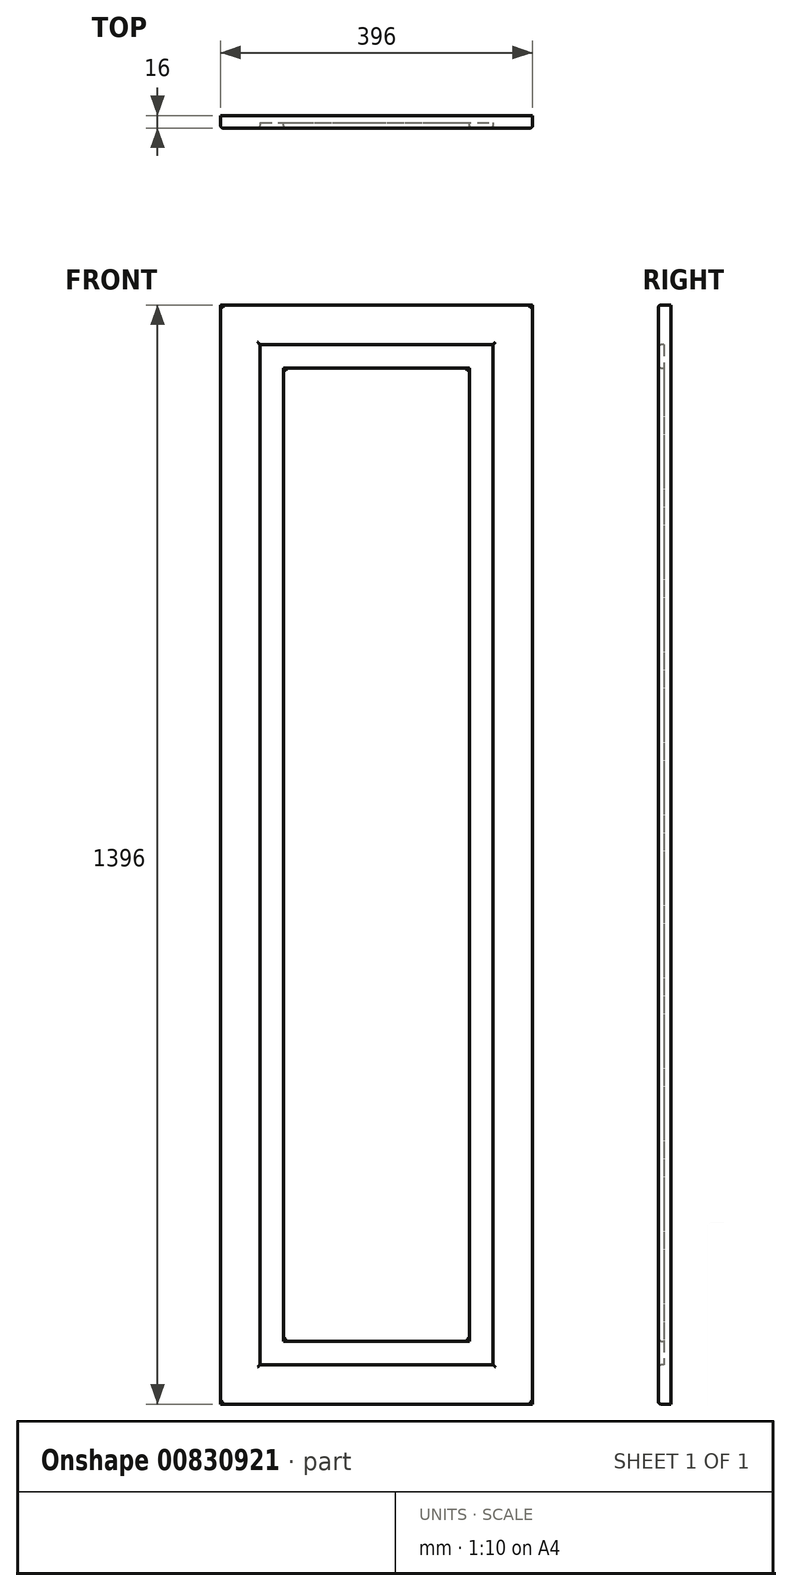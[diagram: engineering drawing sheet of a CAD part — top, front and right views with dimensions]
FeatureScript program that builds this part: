
annotation { "Feature Type Name" : "Feature", "Feature Type Description" : "" }
export const myFeature = defineFeature(function(context is Context, id is Id, definition is map)
    precondition{}
    {
        {
            var Q0;
            Q0=qCreatedBy(makeId("Front.planeOp"),FACE);
            var sketch = newSketch(context, id + "F0", { "sketchPlane" : qUnion([Q0])});
            skLineSegment(sketch, "E0.bottom", {"start": v(0, 0) * mm, "end": v(44.66, 0) * mm});
            skLineSegment(sketch, "E0.top", {"start": v(0, 33.8) * mm, "end": v(44.66, 33.8) * mm});
            skLineSegment(sketch, "E0.left", {"start": v(0, 0) * mm, "end": v(0, 33.8) * mm});
            skLineSegment(sketch, "E0.right", {"start": v(44.66, 0) * mm, "end": v(44.66, 33.8) * mm});
            skSolve(sketch);
        }
        {
            var Q0;
            Q0=makeQuery(id+"F0.imprint","IMPRINT",FACE,{"disambiguationData":[TD([[makeQuery(id+"F0.imprint","IMPRINT",EDGE,{"derivedFrom":sQuery(id+"F0.wireOp",EDGE,"E0.bottom")}),1.0]])]});
            extrude(context, id + "F1", {"entities" : qUnion([Q0]), "depth" : 16 * mm, "offsetDistance" : 25.4 * mm});
        }
        {
            var Q0;
            Q0=makeQuery(id+"F1.opExtrude","SWEPT_FACE",FACE,{"disambiguationData":[OSD([sQuery(id+"F0.wireOp",EDGE,"E0.bottom")])]});
            extrude(context, id + "F2", {"entities" : qUnion([Q0]), "operationType" : NewBodyOperationType.ADD, "oppositeDirection" : true, "depth" : 796 * mm, "offsetDistance" : 25 * mm});
        }
        {
            var Q0;
            {var subQ0=sQuery(id+"F0.wireOp",EDGE,"E0.left");Q0=makeQuery(id+"F2.boolean.opBoolean","MERGE",FACE,{"derivedFrom":[makeQuery(id+"F1.opExtrude","SWEPT_FACE",FACE,{"disambiguationData":[OSD([subQ0])]}),makeQuery(id+"F2.opExtrude","SWEPT_FACE",FACE,{"disambiguationData":[OSD([sQuery(id+"F0.wireOp",EDGE,"E0.bottom"),subQ0])]})]});}
            extrude(context, id + "F3", {"entities" : qUnion([Q0]), "operationType" : NewBodyOperationType.ADD, "oppositeDirection" : true, "depth" : 196 * mm, "offsetDistance" : 25 * mm});
        }
        {
            var Q0;
            {var subQ0=sQuery(id+"F0.wireOp",EDGE,"E0.left");var subQ1=sQuery(id+"F0.wireOp",EDGE,"E0.bottom");Q0=makeQuery(id+"F3.boolean.opBoolean","MERGE",FACE,{"derivedFrom":[makeQuery(id+"F2.boolean.opBoolean","MERGE",FACE,{"derivedFrom":[makeQuery(id+"F1.opExtrude","CAP_FACE",FACE,{"disambiguationData":[OSD([subQ1,sQuery(id+"F0.wireOp",EDGE,"E0.top"),subQ0,sQuery(id+"F0.wireOp",EDGE,"E0.right")])],"isStart":false}),makeQuery(id+"F2.opExtrude","SWEPT_FACE",FACE,{"disambiguationData":[OSD([subQ1]),TDD([makeQuery(id+"F1.opExtrude","CAP_EDGE",EDGE,{"disambiguationData":[OSD([subQ1])],"isStart":false})])]})]}),makeQuery(id+"F3.opExtrude","SWEPT_FACE",FACE,{"disambiguationData":[OSD([subQ1,subQ0]),TDD([makeQuery(id+"F2.boolean.opBoolean","MERGE",EDGE,{"derivedFrom":[makeQuery(id+"F1.opExtrude","CAP_EDGE",EDGE,{"disambiguationData":[OSD([subQ0])],"isStart":false}),makeQuery(id+"F2.opExtrude","SWEPT_EDGE",EDGE,{"disambiguationData":[OSD([subQ1,subQ0]),TDD([makeQuery(id+"F1.opExtrude","CAP_VERTEX",VERTEX,{"disambiguationData":[OSD([subQ1,subQ0])],"isStart":false})])]})]})])]})]});}
            var sketch = newSketch(context, id + "F4", { "sketchPlane" : qUnion([Q0])});
            skLineSegment(sketch, "E1.bottom", {"start": v(59.7, 646.67) * mm, "end": v(128.66, 646.67) * mm});
            skLineSegment(sketch, "E1.top", {"start": v(59.7, 152.97) * mm, "end": v(128.66, 152.97) * mm});
            skLineSegment(sketch, "E1.left", {"start": v(59.7, 646.67) * mm, "end": v(59.7, 152.97) * mm});
            skLineSegment(sketch, "E1.right", {"start": v(128.66, 646.67) * mm, "end": v(128.66, 152.97) * mm});
            skSolve(sketch);
        }
        {
            var Q0;
            Q0=makeQuery(id+"F4.imprint","IMPRINT",FACE,{"disambiguationData":[TD([[makeQuery(id+"F4.imprint","IMPRINT",EDGE,{"derivedFrom":sQuery(id+"F4.wireOp",EDGE,"E1.bottom")}),-1.0]])]});
            extrude(context, id + "F5", {"entities" : qUnion([Q0]), "operationType" : NewBodyOperationType.REMOVE, "oppositeDirection" : true, "depth" : 7 * mm, "offsetDistance" : 25 * mm});
        }
        {
            var Q0;
            Q0=makeQuery(id+"F5.boolean.opBoolean","COPY",FACE,{"derivedFrom":makeQuery(id+"F5.opExtrude","SWEPT_FACE",FACE,{"disambiguationData":[OSD([sQuery(id+"F4.wireOp",EDGE,"E1.left")])]})});
            extrude(context, id + "F6", {"entities" : qUnion([Q0]), "operationType" : NewBodyOperationType.REMOVE, "oppositeDirection" : true, "depth" : 9.7 * mm, "offsetDistance" : 25 * mm});
        }
        {
            var Q0;
            {var subQ0=sQuery(id+"F4.wireOp",EDGE,"E1.bottom");Q0=makeQuery(id+"F6.boolean.opBoolean","MERGE",FACE,{"derivedFrom":[makeQuery(id+"F5.boolean.opBoolean","COPY",FACE,{"derivedFrom":makeQuery(id+"F5.opExtrude","SWEPT_FACE",FACE,{"disambiguationData":[OSD([subQ0])]})}),makeQuery(id+"F6.opExtrude","SWEPT_FACE",FACE,{"disambiguationData":[OSD([subQ0,sQuery(id+"F4.wireOp",EDGE,"E1.left")])]})]});}
            extrude(context, id + "F7", {"entities" : qUnion([Q0]), "operationType" : NewBodyOperationType.ADD, "oppositeDirection" : true, "depth" : 99.33 * mm, "offsetDistance" : 25 * mm});
        }
        {
            var Q0;
            {var subQ0=sQuery(id+"F4.wireOp",EDGE,"E1.bottom");Q0=makeQuery(id+"F6.boolean.opBoolean","MERGE",FACE,{"derivedFrom":[makeQuery(id+"F5.boolean.opBoolean","COPY",FACE,{"derivedFrom":makeQuery(id+"F5.opExtrude","SWEPT_FACE",FACE,{"disambiguationData":[OSD([subQ0])]})}),makeQuery(id+"F6.opExtrude","SWEPT_FACE",FACE,{"disambiguationData":[OSD([subQ0,sQuery(id+"F4.wireOp",EDGE,"E1.left")])]})]});}
            extrude(context, id + "F8", {"entities" : qUnion([Q0]), "operationType" : NewBodyOperationType.REMOVE, "oppositeDirection" : true, "depth" : 99.33 * mm, "offsetDistance" : 25 * mm});
        }
        {
            var Q0;
            {var subQ0=sQuery(id+"F4.wireOp",EDGE,"E1.right");Q0=makeQuery(id+"F8.boolean.opBoolean","MERGE",FACE,{"derivedFrom":[makeQuery(id+"F5.boolean.opBoolean","COPY",FACE,{"derivedFrom":makeQuery(id+"F5.opExtrude","SWEPT_FACE",FACE,{"disambiguationData":[OSD([subQ0])]})}),makeQuery(id+"F8.opExtrude","SWEPT_FACE",FACE,{"disambiguationData":[OSD([sQuery(id+"F4.wireOp",EDGE,"E1.bottom"),subQ0])]})]});}
            extrude(context, id + "F9", {"entities" : qUnion([Q0]), "operationType" : NewBodyOperationType.REMOVE, "oppositeDirection" : true, "depth" : 17.34 * mm, "offsetDistance" : 25 * mm});
        }
        {
            var Q0;
            {var subQ0=sQuery(id+"F4.wireOp",EDGE,"E1.top");Q0=makeQuery(id+"F9.boolean.opBoolean","MERGE",FACE,{"derivedFrom":[makeQuery(id+"F6.boolean.opBoolean","MERGE",FACE,{"derivedFrom":[makeQuery(id+"F5.boolean.opBoolean","COPY",FACE,{"derivedFrom":makeQuery(id+"F5.opExtrude","SWEPT_FACE",FACE,{"disambiguationData":[OSD([subQ0])]})}),makeQuery(id+"F6.opExtrude","SWEPT_FACE",FACE,{"disambiguationData":[OSD([subQ0,sQuery(id+"F4.wireOp",EDGE,"E1.left")])]})]}),makeQuery(id+"F9.opExtrude","SWEPT_FACE",FACE,{"disambiguationData":[OSD([subQ0,sQuery(id+"F4.wireOp",EDGE,"E1.right")])]})]});}
            extrude(context, id + "F10", {"entities" : qUnion([Q0]), "operationType" : NewBodyOperationType.REMOVE, "oppositeDirection" : true, "depth" : 102.97 * mm, "offsetDistance" : 25 * mm});
        }
        {
            var Q0;
            {var subQ0=sQuery(id+"F4.wireOp",EDGE,"E1.right");var subQ1=sQuery(id+"F4.wireOp",EDGE,"E1.top");var subQ2=sQuery(id+"F4.wireOp",EDGE,"E1.left");var subQ3=sQuery(id+"F4.wireOp",EDGE,"E1.bottom");Q0=makeQuery(id+"F10.boolean.opBoolean","MERGE",FACE,{"derivedFrom":[makeQuery(id+"F9.boolean.opBoolean","MERGE",FACE,{"derivedFrom":[makeQuery(id+"F8.boolean.opBoolean","MERGE",FACE,{"derivedFrom":[makeQuery(id+"F6.boolean.opBoolean","MERGE",FACE,{"derivedFrom":[makeQuery(id+"F5.boolean.opBoolean","COPY",FACE,{"derivedFrom":makeQuery(id+"F5.opExtrude","CAP_FACE",FACE,{"disambiguationData":[OSD([subQ3,subQ1,subQ2,subQ0])],"isStart":false})}),makeQuery(id+"F6.opExtrude","SWEPT_FACE",FACE,{"disambiguationData":[OSD([subQ2]),TDD([makeQuery(id+"F5.boolean.opBoolean","COPY",EDGE,{"derivedFrom":makeQuery(id+"F5.opExtrude","CAP_EDGE",EDGE,{"disambiguationData":[OSD([subQ2])],"isStart":false})})])]})]}),makeQuery(id+"F8.opExtrude","SWEPT_FACE",FACE,{"disambiguationData":[OSD([subQ3,subQ2]),TDD([makeQuery(id+"F6.boolean.opBoolean","MERGE",EDGE,{"derivedFrom":[makeQuery(id+"F5.boolean.opBoolean","COPY",EDGE,{"derivedFrom":makeQuery(id+"F5.opExtrude","CAP_EDGE",EDGE,{"disambiguationData":[OSD([subQ3])],"isStart":false})}),makeQuery(id+"F6.opExtrude","SWEPT_EDGE",EDGE,{"disambiguationData":[OSD([subQ3,subQ2]),TDD([makeQuery(id+"F5.boolean.opBoolean","COPY",VERTEX,{"derivedFrom":makeQuery(id+"F5.opExtrude","CAP_VERTEX",VERTEX,{"disambiguationData":[OSD([subQ3,subQ2])],"isStart":false})})])]})]})])]})]}),makeQuery(id+"F9.opExtrude","SWEPT_FACE",FACE,{"disambiguationData":[OSD([subQ3,subQ0]),TDD([makeQuery(id+"F8.boolean.opBoolean","MERGE",EDGE,{"derivedFrom":[makeQuery(id+"F5.boolean.opBoolean","COPY",EDGE,{"derivedFrom":makeQuery(id+"F5.opExtrude","CAP_EDGE",EDGE,{"disambiguationData":[OSD([subQ0])],"isStart":false})}),makeQuery(id+"F8.opExtrude","SWEPT_EDGE",EDGE,{"disambiguationData":[OSD([subQ3,subQ0]),TDD([makeQuery(id+"F5.boolean.opBoolean","COPY",VERTEX,{"derivedFrom":makeQuery(id+"F5.opExtrude","CAP_VERTEX",VERTEX,{"disambiguationData":[OSD([subQ3,subQ0])],"isStart":false})})])]})]})])]})]}),makeQuery(id+"F10.opExtrude","SWEPT_FACE",FACE,{"disambiguationData":[OSD([subQ1,subQ2,subQ0]),TDD([makeQuery(id+"F9.boolean.opBoolean","MERGE",EDGE,{"derivedFrom":[makeQuery(id+"F6.boolean.opBoolean","MERGE",EDGE,{"derivedFrom":[makeQuery(id+"F5.boolean.opBoolean","COPY",EDGE,{"derivedFrom":makeQuery(id+"F5.opExtrude","CAP_EDGE",EDGE,{"disambiguationData":[OSD([subQ1])],"isStart":false})}),makeQuery(id+"F6.opExtrude","SWEPT_EDGE",EDGE,{"disambiguationData":[OSD([subQ1,subQ2]),TDD([makeQuery(id+"F5.boolean.opBoolean","COPY",VERTEX,{"derivedFrom":makeQuery(id+"F5.opExtrude","CAP_VERTEX",VERTEX,{"disambiguationData":[OSD([subQ1,subQ2])],"isStart":false})})])]})]}),makeQuery(id+"F9.opExtrude","SWEPT_EDGE",EDGE,{"disambiguationData":[OSD([subQ1,subQ0]),TDD([makeQuery(id+"F5.boolean.opBoolean","COPY",VERTEX,{"derivedFrom":makeQuery(id+"F5.opExtrude","CAP_VERTEX",VERTEX,{"disambiguationData":[OSD([subQ1,subQ0])],"isStart":false})})])]})]})])]})]});}
            var sketch = newSketch(context, id + "F11", { "sketchPlane" : qUnion([Q0])});
            skLineSegment(sketch, "E2.bottom", {"start": v(74.13, 678.73) * mm, "end": v(109.41, 678.73) * mm});
            skLineSegment(sketch, "E2.top", {"start": v(74.13, 186.63) * mm, "end": v(109.41, 186.63) * mm});
            skLineSegment(sketch, "E2.left", {"start": v(74.13, 678.73) * mm, "end": v(74.13, 186.63) * mm});
            skLineSegment(sketch, "E2.right", {"start": v(109.41, 678.73) * mm, "end": v(109.41, 186.63) * mm});
            skSolve(sketch);
        }
        {
            var Q0;
            Q0=makeQuery(id+"F11.imprint","IMPRINT",FACE,{"disambiguationData":[TD([[makeQuery(id+"F11.imprint","IMPRINT",EDGE,{"derivedFrom":sQuery(id+"F11.wireOp",EDGE,"E2.bottom")}),-1.0]])]});
            extrude(context, id + "F12", {"entities" : qUnion([Q0]), "operationType" : NewBodyOperationType.ADD, "depth" : 7 * mm, "offsetDistance" : 25 * mm});
        }
        {
            var Q0;
            Q0=makeQuery(id+"F12.opExtrude","SWEPT_FACE",FACE,{"disambiguationData":[OSD([sQuery(id+"F11.wireOp",EDGE,"E2.bottom")])]});
            extrude(context, id + "F13", {"entities" : qUnion([Q0]), "operationType" : NewBodyOperationType.ADD, "depth" : 37.27 * mm, "offsetDistance" : 25 * mm});
        }
        {
            var Q0;
            {var subQ0=sQuery(id+"F11.wireOp",EDGE,"E2.right");Q0=makeQuery(id+"F13.boolean.opBoolean","MERGE",FACE,{"derivedFrom":[makeQuery(id+"F12.opExtrude","SWEPT_FACE",FACE,{"disambiguationData":[OSD([subQ0])]}),makeQuery(id+"F13.opExtrude","SWEPT_FACE",FACE,{"disambiguationData":[OSD([sQuery(id+"F11.wireOp",EDGE,"E2.bottom"),subQ0])]})]});}
            extrude(context, id + "F14", {"entities" : qUnion([Q0]), "operationType" : NewBodyOperationType.ADD, "depth" : 6.58 * mm, "offsetDistance" : 25 * mm});
        }
        {
            var Q0;
            {var subQ0=sQuery(id+"F11.wireOp",EDGE,"E2.top");Q0=makeQuery(id+"F14.boolean.opBoolean","MERGE",FACE,{"derivedFrom":[makeQuery(id+"F12.opExtrude","SWEPT_FACE",FACE,{"disambiguationData":[OSD([subQ0])]}),makeQuery(id+"F14.opExtrude","SWEPT_FACE",FACE,{"disambiguationData":[OSD([subQ0,sQuery(id+"F11.wireOp",EDGE,"E2.right")])]})]});}
            extrude(context, id + "F15", {"entities" : qUnion([Q0]), "operationType" : NewBodyOperationType.ADD, "depth" : 106.63 * mm, "offsetDistance" : 25 * mm});
        }
        {
            var Q0;
            {var subQ0=sQuery(id+"F11.wireOp",EDGE,"E2.left");Q0=makeQuery(id+"F15.boolean.opBoolean","MERGE",FACE,{"derivedFrom":[makeQuery(id+"F13.boolean.opBoolean","MERGE",FACE,{"derivedFrom":[makeQuery(id+"F12.opExtrude","SWEPT_FACE",FACE,{"disambiguationData":[OSD([subQ0])]}),makeQuery(id+"F13.opExtrude","SWEPT_FACE",FACE,{"disambiguationData":[OSD([sQuery(id+"F11.wireOp",EDGE,"E2.bottom"),subQ0])]})]}),makeQuery(id+"F15.opExtrude","SWEPT_FACE",FACE,{"disambiguationData":[OSD([sQuery(id+"F11.wireOp",EDGE,"E2.top"),subQ0])]})]});}
            extrude(context, id + "F16", {"entities" : qUnion([Q0]), "operationType" : NewBodyOperationType.REMOVE, "oppositeDirection" : true, "depth" : 5.87 * mm, "offsetDistance" : 25 * mm});
        }
        {
            var Q0;
            Q0=makeQuery(id+"F3.opExtrude","CAP_FACE",FACE,{"disambiguationData":[OSD([sQuery(id+"F0.wireOp",EDGE,"E0.bottom"),sQuery(id+"F0.wireOp",EDGE,"E0.left")])],"isStart":false});
            extrude(context, id + "F17", {"entities" : qUnion([Q0]), "operationType" : NewBodyOperationType.ADD, "depth" : 200 * mm, "offsetDistance" : 25 * mm});
        }
        {
            var Q0;
            {var subQ0=sQuery(id+"F4.wireOp",EDGE,"E1.right");Q0=makeQuery(id+"F10.boolean.opBoolean","MERGE",FACE,{"derivedFrom":[makeQuery(id+"F9.boolean.opBoolean","COPY",FACE,{"derivedFrom":makeQuery(id+"F9.opExtrude","CAP_FACE",FACE,{"disambiguationData":[OSD([sQuery(id+"F4.wireOp",EDGE,"E1.bottom"),subQ0])],"isStart":false})}),makeQuery(id+"F10.opExtrude","SWEPT_FACE",FACE,{"disambiguationData":[OSD([sQuery(id+"F4.wireOp",EDGE,"E1.top"),subQ0])]})]});}
            extrude(context, id + "F18", {"entities" : qUnion([Q0]), "operationType" : NewBodyOperationType.REMOVE, "oppositeDirection" : true, "depth" : 200 * mm, "offsetDistance" : 25 * mm});
        }
        {
            var Q0;
            {var subQ0=sQuery(id+"F11.wireOp",EDGE,"E2.right");var subQ1=sQuery(id+"F11.wireOp",EDGE,"E2.top");Q0=makeQuery(id+"F15.boolean.opBoolean","MERGE",FACE,{"derivedFrom":[makeQuery(id+"F14.opExtrude","CAP_FACE",FACE,{"disambiguationData":[OSD([sQuery(id+"F11.wireOp",EDGE,"E2.bottom"),subQ0])],"isStart":false}),makeQuery(id+"F15.opExtrude","SWEPT_FACE",FACE,{"disambiguationData":[OSD([subQ1,subQ0]),TDD([makeQuery(id+"F14.opExtrude","CAP_EDGE",EDGE,{"disambiguationData":[OSD([subQ1,subQ0])],"isStart":false})])]})]});}
            extrude(context, id + "F19", {"entities" : qUnion([Q0]), "operationType" : NewBodyOperationType.ADD, "depth" : 200 * mm, "offsetDistance" : 25 * mm});
        }
        {
            var Q0;
            Q0=makeQuery(id+"F17.opExtrude","CAP_FACE",FACE,{"disambiguationData":[OSD([sQuery(id+"F0.wireOp",EDGE,"E0.bottom"),sQuery(id+"F0.wireOp",EDGE,"E0.left")])],"isStart":false});
            extrude(context, id + "F20", {"entities" : qUnion([Q0]), "operationType" : NewBodyOperationType.ADD, "depth" : 200 * mm, "offsetDistance" : 25 * mm});
        }
        {
            var Q0;
            Q0=makeQuery(id+"F18.boolean.opBoolean","COPY",FACE,{"derivedFrom":makeQuery(id+"F18.opExtrude","CAP_FACE",FACE,{"disambiguationData":[OSD([sQuery(id+"F4.wireOp",EDGE,"E1.bottom"),sQuery(id+"F4.wireOp",EDGE,"E1.top"),sQuery(id+"F4.wireOp",EDGE,"E1.right")])],"isStart":false})});
            extrude(context, id + "F21", {"entities" : qUnion([Q0]), "operationType" : NewBodyOperationType.REMOVE, "oppositeDirection" : true, "depth" : 200 * mm, "offsetDistance" : 25 * mm});
        }
        {
            var Q0;
            Q0=makeQuery(id+"F19.opExtrude","CAP_FACE",FACE,{"disambiguationData":[OSD([sQuery(id+"F11.wireOp",EDGE,"E2.bottom"),sQuery(id+"F11.wireOp",EDGE,"E2.top"),sQuery(id+"F11.wireOp",EDGE,"E2.right")])],"isStart":false});
            extrude(context, id + "F22", {"entities" : qUnion([Q0]), "operationType" : NewBodyOperationType.ADD, "depth" : 200 * mm, "offsetDistance" : 25 * mm});
        }
        {
            var Q0;
            Q0=makeQuery(id+"F20.opExtrude","CAP_FACE",FACE,{"disambiguationData":[OSD([sQuery(id+"F0.wireOp",EDGE,"E0.bottom"),sQuery(id+"F0.wireOp",EDGE,"E0.left")])],"isStart":false});
            extrude(context, id + "F23", {"entities" : qUnion([Q0]), "operationType" : NewBodyOperationType.ADD, "depth" : 400 * mm, "offsetDistance" : 25 * mm});
        }
        {
            var Q0;
            Q0=makeQuery(id+"F21.boolean.opBoolean","COPY",FACE,{"derivedFrom":makeQuery(id+"F21.opExtrude","CAP_FACE",FACE,{"disambiguationData":[OSD([sQuery(id+"F4.wireOp",EDGE,"E1.bottom"),sQuery(id+"F4.wireOp",EDGE,"E1.top"),sQuery(id+"F4.wireOp",EDGE,"E1.right")])],"isStart":false})});
            extrude(context, id + "F24", {"entities" : qUnion([Q0]), "operationType" : NewBodyOperationType.REMOVE, "oppositeDirection" : true, "depth" : 400 * mm, "offsetDistance" : 25 * mm});
        }
        {
            var Q0;
            Q0=makeQuery(id+"F22.opExtrude","CAP_FACE",FACE,{"disambiguationData":[OSD([sQuery(id+"F11.wireOp",EDGE,"E2.bottom"),sQuery(id+"F11.wireOp",EDGE,"E2.top"),sQuery(id+"F11.wireOp",EDGE,"E2.right")])],"isStart":false});
            extrude(context, id + "F25", {"entities" : qUnion([Q0]), "operationType" : NewBodyOperationType.ADD, "depth" : 400 * mm, "offsetDistance" : 25 * mm});
        }
        {
            var Q0;
            {var subQ0=sQuery(id+"F11.wireOp",EDGE,"E2.right");var subQ1=sQuery(id+"F11.wireOp",EDGE,"E2.top");Q0=makeQuery(id+"F25.boolean.opBoolean","MERGE",FACE,{"derivedFrom":[makeQuery(id+"F22.boolean.opBoolean","MERGE",FACE,{"derivedFrom":[makeQuery(id+"F19.boolean.opBoolean","MERGE",FACE,{"derivedFrom":[makeQuery(id+"F15.opExtrude","CAP_FACE",FACE,{"disambiguationData":[OSD([subQ1,subQ0])],"isStart":false}),makeQuery(id+"F19.opExtrude","SWEPT_FACE",FACE,{"disambiguationData":[OSD([subQ1,subQ0])]})]}),makeQuery(id+"F22.opExtrude","SWEPT_FACE",FACE,{"disambiguationData":[OSD([subQ1,subQ0])]})]}),makeQuery(id+"F25.opExtrude","SWEPT_FACE",FACE,{"disambiguationData":[OSD([subQ1,subQ0])]})]});}
            extrude(context, id + "F26", {"entities" : qUnion([Q0]), "operationType" : NewBodyOperationType.REMOVE, "oppositeDirection" : true, "depth" : 400 * mm, "offsetDistance" : 25 * mm});
        }
        {
            var Q0;
            {var subQ0=sQuery(id+"F4.wireOp",EDGE,"E1.right");var subQ1=sQuery(id+"F4.wireOp",EDGE,"E1.top");Q0=makeQuery(id+"F24.boolean.opBoolean","MERGE",FACE,{"derivedFrom":[makeQuery(id+"F21.boolean.opBoolean","MERGE",FACE,{"derivedFrom":[makeQuery(id+"F18.boolean.opBoolean","MERGE",FACE,{"derivedFrom":[makeQuery(id+"F10.boolean.opBoolean","COPY",FACE,{"derivedFrom":makeQuery(id+"F10.opExtrude","CAP_FACE",FACE,{"disambiguationData":[OSD([subQ1,sQuery(id+"F4.wireOp",EDGE,"E1.left"),subQ0])],"isStart":false})}),makeQuery(id+"F18.opExtrude","SWEPT_FACE",FACE,{"disambiguationData":[OSD([subQ1,subQ0])]})]}),makeQuery(id+"F21.opExtrude","SWEPT_FACE",FACE,{"disambiguationData":[OSD([subQ1,subQ0])]})]}),makeQuery(id+"F24.opExtrude","SWEPT_FACE",FACE,{"disambiguationData":[OSD([subQ1,subQ0])]})]});}
            extrude(context, id + "F27", {"entities" : qUnion([Q0]), "operationType" : NewBodyOperationType.ADD, "depth" : 400 * mm, "offsetDistance" : 25 * mm});
        }
        {
            var Q0;
            {var subQ0=sQuery(id+"F0.wireOp",EDGE,"E0.left");var subQ1=sQuery(id+"F0.wireOp",EDGE,"E0.bottom");var subQ2=makeQuery(id+"F1.opExtrude","SWEPT_EDGE",EDGE,{"disambiguationData":[OSD([subQ1,subQ0])]});var subQ3=makeQuery(id+"F3.opExtrude","CAP_EDGE",EDGE,{"disambiguationData":[OSD([subQ1,subQ0]),TDD([subQ2])],"isStart":false});var subQ4=makeQuery(id+"F17.opExtrude","CAP_EDGE",EDGE,{"disambiguationData":[OSD([subQ1,subQ0]),TDD([subQ3])],"isStart":false});Q0=makeQuery(id+"F23.boolean.opBoolean","MERGE",FACE,{"derivedFrom":[makeQuery(id+"F20.boolean.opBoolean","MERGE",FACE,{"derivedFrom":[makeQuery(id+"F17.boolean.opBoolean","MERGE",FACE,{"derivedFrom":[makeQuery(id+"F3.boolean.opBoolean","MERGE",FACE,{"derivedFrom":[makeQuery(id+"F1.opExtrude","SWEPT_FACE",FACE,{"disambiguationData":[OSD([subQ1])]}),makeQuery(id+"F3.opExtrude","SWEPT_FACE",FACE,{"disambiguationData":[OSD([subQ1,subQ0]),TDD([subQ2])]})]}),makeQuery(id+"F17.opExtrude","SWEPT_FACE",FACE,{"disambiguationData":[OSD([subQ1,subQ0]),TDD([subQ3])]})]}),makeQuery(id+"F20.opExtrude","SWEPT_FACE",FACE,{"disambiguationData":[OSD([subQ1,subQ0]),TDD([subQ4])]})]}),makeQuery(id+"F23.opExtrude","SWEPT_FACE",FACE,{"disambiguationData":[OSD([subQ1,subQ0]),TDD([makeQuery(id+"F20.opExtrude","CAP_EDGE",EDGE,{"disambiguationData":[OSD([subQ1,subQ0]),TDD([subQ4])],"isStart":false})])]})]});}
            extrude(context, id + "F28", {"entities" : qUnion([Q0]), "operationType" : NewBodyOperationType.REMOVE, "oppositeDirection" : true, "depth" : 400 * mm, "offsetDistance" : 25 * mm});
        }
        {
            var Q0;
            Q0=makeQuery(id+"F23.opExtrude","CAP_FACE",FACE,{"disambiguationData":[OSD([sQuery(id+"F0.wireOp",EDGE,"E0.bottom"),sQuery(id+"F0.wireOp",EDGE,"E0.left")])],"isStart":false});
            extrude(context, id + "F29", {"entities" : qUnion([Q0]), "operationType" : NewBodyOperationType.ADD, "depth" : 400 * mm, "offsetDistance" : 25 * mm});
        }
        {
            var Q0;
            Q0=makeQuery(id+"F24.boolean.opBoolean","COPY",FACE,{"derivedFrom":makeQuery(id+"F24.opExtrude","CAP_FACE",FACE,{"disambiguationData":[OSD([sQuery(id+"F4.wireOp",EDGE,"E1.bottom"),sQuery(id+"F4.wireOp",EDGE,"E1.top"),sQuery(id+"F4.wireOp",EDGE,"E1.right")])],"isStart":false})});
            extrude(context, id + "F30", {"entities" : qUnion([Q0]), "operationType" : NewBodyOperationType.REMOVE, "oppositeDirection" : true, "depth" : 400 * mm, "offsetDistance" : 25 * mm});
        }
        {
            var Q0;
            Q0=makeQuery(id+"F25.opExtrude","CAP_FACE",FACE,{"disambiguationData":[OSD([sQuery(id+"F11.wireOp",EDGE,"E2.bottom"),sQuery(id+"F11.wireOp",EDGE,"E2.top"),sQuery(id+"F11.wireOp",EDGE,"E2.right")])],"isStart":false});
            extrude(context, id + "F31", {"entities" : qUnion([Q0]), "operationType" : NewBodyOperationType.ADD, "depth" : 400 * mm, "offsetDistance" : 25 * mm});
        }
        {
            var Q0;
            Q0=makeQuery(id+"F31.opExtrude","CAP_FACE",FACE,{"disambiguationData":[OSD([sQuery(id+"F11.wireOp",EDGE,"E2.bottom"),sQuery(id+"F11.wireOp",EDGE,"E2.top"),sQuery(id+"F11.wireOp",EDGE,"E2.right")])],"isStart":false});
            extrude(context, id + "F32", {"entities" : qUnion([Q0]), "operationType" : NewBodyOperationType.REMOVE, "oppositeDirection" : true, "depth" : 1000 * mm, "offsetDistance" : 25 * mm});
        }
        {
            var Q0;
            Q0=makeQuery(id+"F30.boolean.opBoolean","COPY",FACE,{"derivedFrom":makeQuery(id+"F30.opExtrude","CAP_FACE",FACE,{"disambiguationData":[OSD([sQuery(id+"F4.wireOp",EDGE,"E1.bottom"),sQuery(id+"F4.wireOp",EDGE,"E1.top"),sQuery(id+"F4.wireOp",EDGE,"E1.right")])],"isStart":false})});
            extrude(context, id + "F33", {"entities" : qUnion([Q0]), "operationType" : NewBodyOperationType.ADD, "depth" : 1000 * mm, "offsetDistance" : 25 * mm});
        }
        {
            var Q0;
            Q0=makeQuery(id+"F29.opExtrude","CAP_FACE",FACE,{"disambiguationData":[OSD([sQuery(id+"F0.wireOp",EDGE,"E0.bottom"),sQuery(id+"F0.wireOp",EDGE,"E0.left")])],"isStart":false});
            extrude(context, id + "F34", {"entities" : qUnion([Q0]), "operationType" : NewBodyOperationType.REMOVE, "oppositeDirection" : true, "depth" : 1000 * mm, "offsetDistance" : 25 * mm});
        }
        {
            var Q0;
            {var subQ0=sQuery(id+"F0.wireOp",EDGE,"E0.left");var subQ1=sQuery(id+"F0.wireOp",EDGE,"E0.bottom");var subQ2=makeQuery(id+"F2.opExtrude","CAP_EDGE",EDGE,{"disambiguationData":[OSD([subQ1,subQ0])],"isStart":false});var subQ3=makeQuery(id+"F3.opExtrude","CAP_EDGE",EDGE,{"disambiguationData":[OSD([subQ1,subQ0]),TDD([subQ2])],"isStart":false});var subQ4=makeQuery(id+"F17.opExtrude","CAP_EDGE",EDGE,{"disambiguationData":[OSD([subQ1,subQ0]),TDD([subQ3])],"isStart":false});var subQ5=makeQuery(id+"F20.opExtrude","CAP_EDGE",EDGE,{"disambiguationData":[OSD([subQ1,subQ0]),TDD([subQ4])],"isStart":false});Q0=makeQuery(id+"F29.boolean.opBoolean","MERGE",FACE,{"derivedFrom":[makeQuery(id+"F23.boolean.opBoolean","MERGE",FACE,{"derivedFrom":[makeQuery(id+"F20.boolean.opBoolean","MERGE",FACE,{"derivedFrom":[makeQuery(id+"F17.boolean.opBoolean","MERGE",FACE,{"derivedFrom":[makeQuery(id+"F3.boolean.opBoolean","MERGE",FACE,{"derivedFrom":[makeQuery(id+"F2.opExtrude","CAP_FACE",FACE,{"disambiguationData":[OSD([subQ1])],"isStart":false}),makeQuery(id+"F3.opExtrude","SWEPT_FACE",FACE,{"disambiguationData":[OSD([subQ1,subQ0]),TDD([subQ2])]})]}),makeQuery(id+"F17.opExtrude","SWEPT_FACE",FACE,{"disambiguationData":[OSD([subQ1,subQ0]),TDD([subQ3])]})]}),makeQuery(id+"F20.opExtrude","SWEPT_FACE",FACE,{"disambiguationData":[OSD([subQ1,subQ0]),TDD([subQ4])]})]}),makeQuery(id+"F23.opExtrude","SWEPT_FACE",FACE,{"disambiguationData":[OSD([subQ1,subQ0]),TDD([subQ5])]})]}),makeQuery(id+"F29.opExtrude","SWEPT_FACE",FACE,{"disambiguationData":[OSD([subQ1,subQ0]),TDD([makeQuery(id+"F23.opExtrude","CAP_EDGE",EDGE,{"disambiguationData":[OSD([subQ1,subQ0]),TDD([subQ5])],"isStart":false})])]})]});}
            extrude(context, id + "F35", {"entities" : qUnion([Q0]), "operationType" : NewBodyOperationType.ADD, "depth" : 1000 * mm, "offsetDistance" : 25 * mm});
        }
        {
            var Q0;
            {var subQ0=sQuery(id+"F4.wireOp",EDGE,"E1.right");var subQ1=sQuery(id+"F4.wireOp",EDGE,"E1.bottom");Q0=makeQuery(id+"F30.boolean.opBoolean","MERGE",FACE,{"derivedFrom":[makeQuery(id+"F24.boolean.opBoolean","MERGE",FACE,{"derivedFrom":[makeQuery(id+"F21.boolean.opBoolean","MERGE",FACE,{"derivedFrom":[makeQuery(id+"F18.boolean.opBoolean","MERGE",FACE,{"derivedFrom":[makeQuery(id+"F9.boolean.opBoolean","MERGE",FACE,{"derivedFrom":[makeQuery(id+"F8.boolean.opBoolean","COPY",FACE,{"derivedFrom":makeQuery(id+"F8.opExtrude","CAP_FACE",FACE,{"disambiguationData":[OSD([subQ1,sQuery(id+"F4.wireOp",EDGE,"E1.left")])],"isStart":false})}),makeQuery(id+"F9.opExtrude","SWEPT_FACE",FACE,{"disambiguationData":[OSD([subQ1,subQ0]),TDD([makeQuery(id+"F8.boolean.opBoolean","COPY",EDGE,{"derivedFrom":makeQuery(id+"F8.opExtrude","CAP_EDGE",EDGE,{"disambiguationData":[OSD([subQ1,subQ0])],"isStart":false})})])]})]}),makeQuery(id+"F18.opExtrude","SWEPT_FACE",FACE,{"disambiguationData":[OSD([subQ1,subQ0])]})]}),makeQuery(id+"F21.opExtrude","SWEPT_FACE",FACE,{"disambiguationData":[OSD([subQ1,subQ0])]})]}),makeQuery(id+"F24.opExtrude","SWEPT_FACE",FACE,{"disambiguationData":[OSD([subQ1,subQ0])]})]}),makeQuery(id+"F30.opExtrude","SWEPT_FACE",FACE,{"disambiguationData":[OSD([subQ1,subQ0])]})]});}
            extrude(context, id + "F36", {"entities" : qUnion([Q0]), "operationType" : NewBodyOperationType.REMOVE, "oppositeDirection" : true, "depth" : 1000 * mm, "offsetDistance" : 25 * mm});
        }
        {
            var Q0;
            {var subQ0=sQuery(id+"F11.wireOp",EDGE,"E2.right");var subQ1=sQuery(id+"F11.wireOp",EDGE,"E2.bottom");Q0=makeQuery(id+"F31.boolean.opBoolean","MERGE",FACE,{"derivedFrom":[makeQuery(id+"F25.boolean.opBoolean","MERGE",FACE,{"derivedFrom":[makeQuery(id+"F22.boolean.opBoolean","MERGE",FACE,{"derivedFrom":[makeQuery(id+"F19.boolean.opBoolean","MERGE",FACE,{"derivedFrom":[makeQuery(id+"F14.boolean.opBoolean","MERGE",FACE,{"derivedFrom":[makeQuery(id+"F13.opExtrude","CAP_FACE",FACE,{"disambiguationData":[OSD([subQ1])],"isStart":false}),makeQuery(id+"F14.opExtrude","SWEPT_FACE",FACE,{"disambiguationData":[OSD([subQ1,subQ0]),TDD([makeQuery(id+"F13.opExtrude","CAP_EDGE",EDGE,{"disambiguationData":[OSD([subQ1,subQ0])],"isStart":false})])]})]}),makeQuery(id+"F19.opExtrude","SWEPT_FACE",FACE,{"disambiguationData":[OSD([subQ1,subQ0])]})]}),makeQuery(id+"F22.opExtrude","SWEPT_FACE",FACE,{"disambiguationData":[OSD([subQ1,subQ0])]})]}),makeQuery(id+"F25.opExtrude","SWEPT_FACE",FACE,{"disambiguationData":[OSD([subQ1,subQ0])]})]}),makeQuery(id+"F31.opExtrude","SWEPT_FACE",FACE,{"disambiguationData":[OSD([subQ1,subQ0])]})]});}
            extrude(context, id + "F37", {"entities" : qUnion([Q0]), "operationType" : NewBodyOperationType.ADD, "depth" : 1000 * mm, "offsetDistance" : 25 * mm});
        }
        {
            var Q0;
            {var subQ0=sQuery(id+"F11.wireOp",EDGE,"E2.right");var subQ1=sQuery(id+"F11.wireOp",EDGE,"E2.bottom");var subQ2=makeQuery(id+"F12.opExtrude","CAP_VERTEX",VERTEX,{"disambiguationData":[OSD([subQ1,subQ0])],"isStart":false});var subQ3=makeQuery(id+"F13.opExtrude","CAP_VERTEX",VERTEX,{"disambiguationData":[OSD([subQ1,subQ0]),TDD([subQ2])],"isStart":false});var subQ4=makeQuery(id+"F14.opExtrude","CAP_VERTEX",VERTEX,{"disambiguationData":[OSD([subQ1,subQ0]),TDD([subQ3])],"isStart":false});var subQ5=makeQuery(id+"F19.opExtrude","CAP_VERTEX",VERTEX,{"disambiguationData":[OSD([subQ1,subQ0]),TDD([subQ4])],"isStart":false});var subQ6=makeQuery(id+"F22.opExtrude","CAP_VERTEX",VERTEX,{"disambiguationData":[OSD([subQ1,subQ0]),TDD([subQ5])],"isStart":false});var subQ7=makeQuery(id+"F12.opExtrude","CAP_EDGE",EDGE,{"disambiguationData":[OSD([subQ1])],"isStart":false});var subQ8=sQuery(id+"F11.wireOp",EDGE,"E2.top");var subQ9=makeQuery(id+"F12.opExtrude","CAP_VERTEX",VERTEX,{"disambiguationData":[OSD([subQ8,subQ0])],"isStart":false});var subQ10=makeQuery(id+"F13.boolean.opBoolean","MERGE",EDGE,{"derivedFrom":[makeQuery(id+"F12.opExtrude","CAP_EDGE",EDGE,{"disambiguationData":[OSD([subQ0])],"isStart":false}),makeQuery(id+"F13.opExtrude","SWEPT_EDGE",EDGE,{"disambiguationData":[OSD([subQ1,subQ0]),TDD([subQ2])]})]});var subQ11=makeQuery(id+"F15.boolean.opBoolean","MERGE",EDGE,{"derivedFrom":[makeQuery(id+"F14.opExtrude","CAP_EDGE",EDGE,{"disambiguationData":[OSD([subQ1,subQ0]),TDD([subQ10])],"isStart":false}),makeQuery(id+"F15.opExtrude","SWEPT_EDGE",EDGE,{"disambiguationData":[OSD([subQ8,subQ0]),TDD([makeQuery(id+"F14.opExtrude","CAP_VERTEX",VERTEX,{"disambiguationData":[OSD([subQ8,subQ0]),TDD([subQ9])],"isStart":false})])]})]});var subQ12=makeQuery(id+"F19.opExtrude","CAP_EDGE",EDGE,{"disambiguationData":[OSD([subQ1,subQ8,subQ0]),TDD([subQ11])],"isStart":false});var subQ13=makeQuery(id+"F22.opExtrude","CAP_EDGE",EDGE,{"disambiguationData":[OSD([subQ1,subQ8,subQ0]),TDD([subQ12])],"isStart":false});Q0=makeQuery(id+"F37.boolean.opBoolean","MERGE",FACE,{"derivedFrom":[makeQuery(id+"F31.boolean.opBoolean","MERGE",FACE,{"derivedFrom":[makeQuery(id+"F25.boolean.opBoolean","MERGE",FACE,{"derivedFrom":[makeQuery(id+"F22.boolean.opBoolean","MERGE",FACE,{"derivedFrom":[makeQuery(id+"F19.boolean.opBoolean","MERGE",FACE,{"derivedFrom":[makeQuery(id+"F15.boolean.opBoolean","MERGE",FACE,{"derivedFrom":[makeQuery(id+"F14.boolean.opBoolean","MERGE",FACE,{"derivedFrom":[makeQuery(id+"F13.boolean.opBoolean","MERGE",FACE,{"derivedFrom":[makeQuery(id+"F12.opExtrude","CAP_FACE",FACE,{"disambiguationData":[OSD([subQ1,subQ8,sQuery(id+"F11.wireOp",EDGE,"E2.left"),subQ0])],"isStart":false}),makeQuery(id+"F13.opExtrude","SWEPT_FACE",FACE,{"disambiguationData":[OSD([subQ1]),TDD([subQ7])]})]}),makeQuery(id+"F14.opExtrude","SWEPT_FACE",FACE,{"disambiguationData":[OSD([subQ1,subQ0]),TDD([subQ10])]})]}),makeQuery(id+"F15.opExtrude","SWEPT_FACE",FACE,{"disambiguationData":[OSD([subQ8,subQ0]),TDD([makeQuery(id+"F14.boolean.opBoolean","MERGE",EDGE,{"derivedFrom":[makeQuery(id+"F12.opExtrude","CAP_EDGE",EDGE,{"disambiguationData":[OSD([subQ8])],"isStart":false}),makeQuery(id+"F14.opExtrude","SWEPT_EDGE",EDGE,{"disambiguationData":[OSD([subQ8,subQ0]),TDD([subQ9])]})]})])]})]}),makeQuery(id+"F19.opExtrude","SWEPT_FACE",FACE,{"disambiguationData":[OSD([subQ1,subQ8,subQ0]),TDD([subQ11])]})]}),makeQuery(id+"F22.opExtrude","SWEPT_FACE",FACE,{"disambiguationData":[OSD([subQ1,subQ8,subQ0]),TDD([subQ12])]})]}),makeQuery(id+"F25.opExtrude","SWEPT_FACE",FACE,{"disambiguationData":[OSD([subQ1,subQ8,subQ0]),TDD([subQ13])]})]}),makeQuery(id+"F31.opExtrude","SWEPT_FACE",FACE,{"disambiguationData":[OSD([subQ1,subQ8,subQ0]),TDD([makeQuery(id+"F25.opExtrude","CAP_EDGE",EDGE,{"disambiguationData":[OSD([subQ1,subQ8,subQ0]),TDD([subQ13])],"isStart":false})])]})]}),makeQuery(id+"F37.opExtrude","SWEPT_FACE",FACE,{"disambiguationData":[OSD([subQ1,subQ0]),TDD([makeQuery(id+"F31.boolean.opBoolean","MERGE",EDGE,{"derivedFrom":[makeQuery(id+"F25.boolean.opBoolean","MERGE",EDGE,{"derivedFrom":[makeQuery(id+"F22.boolean.opBoolean","MERGE",EDGE,{"derivedFrom":[makeQuery(id+"F19.boolean.opBoolean","MERGE",EDGE,{"derivedFrom":[makeQuery(id+"F14.boolean.opBoolean","MERGE",EDGE,{"derivedFrom":[makeQuery(id+"F13.opExtrude","CAP_EDGE",EDGE,{"disambiguationData":[OSD([subQ1]),TDD([subQ7])],"isStart":false}),makeQuery(id+"F14.opExtrude","SWEPT_EDGE",EDGE,{"disambiguationData":[OSD([subQ1,subQ0]),TDD([subQ3])]})]}),makeQuery(id+"F19.opExtrude","SWEPT_EDGE",EDGE,{"disambiguationData":[OSD([subQ1,subQ0]),TDD([subQ4])]})]}),makeQuery(id+"F22.opExtrude","SWEPT_EDGE",EDGE,{"disambiguationData":[OSD([subQ1,subQ0]),TDD([subQ5])]})]}),makeQuery(id+"F25.opExtrude","SWEPT_EDGE",EDGE,{"disambiguationData":[OSD([subQ1,subQ0]),TDD([subQ6])]})]}),makeQuery(id+"F31.opExtrude","SWEPT_EDGE",EDGE,{"disambiguationData":[OSD([subQ1,subQ0]),TDD([makeQuery(id+"F25.opExtrude","CAP_VERTEX",VERTEX,{"disambiguationData":[OSD([subQ1,subQ0]),TDD([subQ6])],"isStart":false})])]})]})])]})]});}
            var Q1;
            {var subQ0=sQuery(id+"F0.wireOp",EDGE,"E0.left");var subQ1=sQuery(id+"F0.wireOp",EDGE,"E0.bottom");var subQ2=makeQuery(id+"F1.opExtrude","CAP_VERTEX",VERTEX,{"disambiguationData":[OSD([subQ1,subQ0])],"isStart":false});var subQ3=makeQuery(id+"F2.opExtrude","CAP_VERTEX",VERTEX,{"disambiguationData":[OSD([subQ1,subQ0]),TDD([subQ2])],"isStart":false});var subQ4=makeQuery(id+"F3.opExtrude","CAP_VERTEX",VERTEX,{"disambiguationData":[OSD([subQ1,subQ0]),TDD([subQ3])],"isStart":false});var subQ5=makeQuery(id+"F17.opExtrude","CAP_VERTEX",VERTEX,{"disambiguationData":[OSD([subQ1,subQ0]),TDD([subQ4])],"isStart":false});var subQ6=makeQuery(id+"F20.opExtrude","CAP_VERTEX",VERTEX,{"disambiguationData":[OSD([subQ1,subQ0]),TDD([subQ5])],"isStart":false});var subQ7=makeQuery(id+"F1.opExtrude","CAP_EDGE",EDGE,{"disambiguationData":[OSD([subQ1])],"isStart":false});var subQ8=sQuery(id+"F4.wireOp",EDGE,"E1.right");var subQ9=sQuery(id+"F4.wireOp",EDGE,"E1.top");var subQ10=makeQuery(id+"F5.boolean.opBoolean","COPY",VERTEX,{"derivedFrom":makeQuery(id+"F5.opExtrude","CAP_VERTEX",VERTEX,{"disambiguationData":[OSD([subQ9,subQ8])],"isStart":true})});var subQ11=makeQuery(id+"F9.boolean.opBoolean","COPY",VERTEX,{"derivedFrom":makeQuery(id+"F9.opExtrude","CAP_VERTEX",VERTEX,{"disambiguationData":[OSD([subQ9,subQ8]),TDD([subQ10])],"isStart":false})});var subQ12=sQuery(id+"F4.wireOp",EDGE,"E1.bottom");var subQ13=makeQuery(id+"F2.boolean.opBoolean","MERGE",EDGE,{"derivedFrom":[makeQuery(id+"F1.opExtrude","CAP_EDGE",EDGE,{"disambiguationData":[OSD([subQ0])],"isStart":false}),makeQuery(id+"F2.opExtrude","SWEPT_EDGE",EDGE,{"disambiguationData":[OSD([subQ1,subQ0]),TDD([subQ2])]})]});var subQ14=makeQuery(id+"F3.opExtrude","CAP_EDGE",EDGE,{"disambiguationData":[OSD([subQ1,subQ0]),TDD([subQ13])],"isStart":false});var subQ15=makeQuery(id+"F17.opExtrude","CAP_EDGE",EDGE,{"disambiguationData":[OSD([subQ1,subQ0]),TDD([subQ14])],"isStart":false});var subQ16=makeQuery(id+"F20.opExtrude","CAP_EDGE",EDGE,{"disambiguationData":[OSD([subQ1,subQ0]),TDD([subQ15])],"isStart":false});var subQ17=makeQuery(id+"F10.boolean.opBoolean","COPY",VERTEX,{"derivedFrom":makeQuery(id+"F10.opExtrude","CAP_VERTEX",VERTEX,{"disambiguationData":[OSD([subQ9,subQ8]),TDD([subQ11])],"isStart":false})});var subQ18=makeQuery(id+"F18.boolean.opBoolean","COPY",VERTEX,{"derivedFrom":makeQuery(id+"F18.opExtrude","CAP_VERTEX",VERTEX,{"disambiguationData":[OSD([subQ9,subQ8]),TDD([subQ17])],"isStart":false})});var subQ19=sQuery(id+"F4.wireOp",EDGE,"E1.left");Q1=makeQuery(id+"F35.boolean.opBoolean","MERGE",FACE,{"derivedFrom":[makeQuery(id+"F33.boolean.opBoolean","MERGE",FACE,{"derivedFrom":[makeQuery(id+"F29.boolean.opBoolean","MERGE",FACE,{"derivedFrom":[makeQuery(id+"F27.boolean.opBoolean","MERGE",FACE,{"derivedFrom":[makeQuery(id+"F23.boolean.opBoolean","MERGE",FACE,{"derivedFrom":[makeQuery(id+"F20.boolean.opBoolean","MERGE",FACE,{"derivedFrom":[makeQuery(id+"F17.boolean.opBoolean","MERGE",FACE,{"derivedFrom":[makeQuery(id+"F3.boolean.opBoolean","MERGE",FACE,{"derivedFrom":[makeQuery(id+"F2.boolean.opBoolean","MERGE",FACE,{"derivedFrom":[makeQuery(id+"F1.opExtrude","CAP_FACE",FACE,{"disambiguationData":[OSD([subQ1,sQuery(id+"F0.wireOp",EDGE,"E0.top"),subQ0,sQuery(id+"F0.wireOp",EDGE,"E0.right")])],"isStart":false}),makeQuery(id+"F2.opExtrude","SWEPT_FACE",FACE,{"disambiguationData":[OSD([subQ1]),TDD([subQ7])]})]}),makeQuery(id+"F3.opExtrude","SWEPT_FACE",FACE,{"disambiguationData":[OSD([subQ1,subQ0]),TDD([subQ13])]})]}),makeQuery(id+"F17.opExtrude","SWEPT_FACE",FACE,{"disambiguationData":[OSD([subQ1,subQ0]),TDD([subQ14])]})]}),makeQuery(id+"F20.opExtrude","SWEPT_FACE",FACE,{"disambiguationData":[OSD([subQ1,subQ0]),TDD([subQ15])]})]}),makeQuery(id+"F23.opExtrude","SWEPT_FACE",FACE,{"disambiguationData":[OSD([subQ1,subQ0]),TDD([subQ16])]})]}),makeQuery(id+"F27.opExtrude","SWEPT_FACE",FACE,{"disambiguationData":[OSD([subQ9,subQ19,subQ8]),TDD([makeQuery(id+"F24.boolean.opBoolean","MERGE",EDGE,{"derivedFrom":[makeQuery(id+"F21.boolean.opBoolean","MERGE",EDGE,{"derivedFrom":[makeQuery(id+"F18.boolean.opBoolean","MERGE",EDGE,{"derivedFrom":[makeQuery(id+"F10.boolean.opBoolean","COPY",EDGE,{"derivedFrom":makeQuery(id+"F10.opExtrude","CAP_EDGE",EDGE,{"disambiguationData":[OSD([subQ9,subQ19,subQ8]),TDD([makeQuery(id+"F9.boolean.opBoolean","MERGE",EDGE,{"derivedFrom":[makeQuery(id+"F6.boolean.opBoolean","MERGE",EDGE,{"derivedFrom":[makeQuery(id+"F5.boolean.opBoolean","COPY",EDGE,{"derivedFrom":makeQuery(id+"F5.opExtrude","CAP_EDGE",EDGE,{"disambiguationData":[OSD([subQ9])],"isStart":true})}),makeQuery(id+"F6.opExtrude","SWEPT_EDGE",EDGE,{"disambiguationData":[OSD([subQ9,subQ19]),TDD([makeQuery(id+"F5.boolean.opBoolean","COPY",VERTEX,{"derivedFrom":makeQuery(id+"F5.opExtrude","CAP_VERTEX",VERTEX,{"disambiguationData":[OSD([subQ9,subQ19])],"isStart":true})})])]})]}),makeQuery(id+"F9.opExtrude","SWEPT_EDGE",EDGE,{"disambiguationData":[OSD([subQ9,subQ8]),TDD([subQ10])]})]})])],"isStart":false})}),makeQuery(id+"F18.opExtrude","SWEPT_EDGE",EDGE,{"disambiguationData":[OSD([subQ9,subQ8]),TDD([subQ17])]})]}),makeQuery(id+"F21.opExtrude","SWEPT_EDGE",EDGE,{"disambiguationData":[OSD([subQ9,subQ8]),TDD([subQ18])]})]}),makeQuery(id+"F24.opExtrude","SWEPT_EDGE",EDGE,{"disambiguationData":[OSD([subQ9,subQ8]),TDD([makeQuery(id+"F21.boolean.opBoolean","COPY",VERTEX,{"derivedFrom":makeQuery(id+"F21.opExtrude","CAP_VERTEX",VERTEX,{"disambiguationData":[OSD([subQ9,subQ8]),TDD([subQ18])],"isStart":false})})])]})]})])]})]}),makeQuery(id+"F29.opExtrude","SWEPT_FACE",FACE,{"disambiguationData":[OSD([subQ1,subQ0]),TDD([makeQuery(id+"F23.opExtrude","CAP_EDGE",EDGE,{"disambiguationData":[OSD([subQ1,subQ0]),TDD([subQ16])],"isStart":false})])]})]}),makeQuery(id+"F33.opExtrude","SWEPT_FACE",FACE,{"disambiguationData":[OSD([subQ12,subQ9,subQ8]),TDD([makeQuery(id+"F30.boolean.opBoolean","COPY",EDGE,{"derivedFrom":makeQuery(id+"F30.opExtrude","CAP_EDGE",EDGE,{"disambiguationData":[OSD([subQ12,subQ9,subQ8]),TDD([makeQuery(id+"F24.boolean.opBoolean","COPY",EDGE,{"derivedFrom":makeQuery(id+"F24.opExtrude","CAP_EDGE",EDGE,{"disambiguationData":[OSD([subQ12,subQ9,subQ8]),TDD([makeQuery(id+"F21.boolean.opBoolean","COPY",EDGE,{"derivedFrom":makeQuery(id+"F21.opExtrude","CAP_EDGE",EDGE,{"disambiguationData":[OSD([subQ12,subQ9,subQ8]),TDD([makeQuery(id+"F18.boolean.opBoolean","COPY",EDGE,{"derivedFrom":makeQuery(id+"F18.opExtrude","CAP_EDGE",EDGE,{"disambiguationData":[OSD([subQ12,subQ9,subQ8]),TDD([makeQuery(id+"F10.boolean.opBoolean","MERGE",EDGE,{"derivedFrom":[makeQuery(id+"F9.boolean.opBoolean","COPY",EDGE,{"derivedFrom":makeQuery(id+"F9.opExtrude","CAP_EDGE",EDGE,{"disambiguationData":[OSD([subQ12,subQ8]),TDD([makeQuery(id+"F8.boolean.opBoolean","MERGE",EDGE,{"derivedFrom":[makeQuery(id+"F5.boolean.opBoolean","COPY",EDGE,{"derivedFrom":makeQuery(id+"F5.opExtrude","CAP_EDGE",EDGE,{"disambiguationData":[OSD([subQ8])],"isStart":true})}),makeQuery(id+"F8.opExtrude","SWEPT_EDGE",EDGE,{"disambiguationData":[OSD([subQ12,subQ8]),TDD([makeQuery(id+"F5.boolean.opBoolean","COPY",VERTEX,{"derivedFrom":makeQuery(id+"F5.opExtrude","CAP_VERTEX",VERTEX,{"disambiguationData":[OSD([subQ12,subQ8])],"isStart":true})})])]})]})])],"isStart":false})}),makeQuery(id+"F10.opExtrude","SWEPT_EDGE",EDGE,{"disambiguationData":[OSD([subQ9,subQ8]),TDD([subQ11])]})]})])],"isStart":false})})])],"isStart":false})})])],"isStart":false})})])],"isStart":false})})])]})]}),makeQuery(id+"F35.opExtrude","SWEPT_FACE",FACE,{"disambiguationData":[OSD([subQ1,subQ0]),TDD([makeQuery(id+"F29.boolean.opBoolean","MERGE",EDGE,{"derivedFrom":[makeQuery(id+"F23.boolean.opBoolean","MERGE",EDGE,{"derivedFrom":[makeQuery(id+"F20.boolean.opBoolean","MERGE",EDGE,{"derivedFrom":[makeQuery(id+"F17.boolean.opBoolean","MERGE",EDGE,{"derivedFrom":[makeQuery(id+"F3.boolean.opBoolean","MERGE",EDGE,{"derivedFrom":[makeQuery(id+"F2.opExtrude","CAP_EDGE",EDGE,{"disambiguationData":[OSD([subQ1]),TDD([subQ7])],"isStart":false}),makeQuery(id+"F3.opExtrude","SWEPT_EDGE",EDGE,{"disambiguationData":[OSD([subQ1,subQ0]),TDD([subQ3])]})]}),makeQuery(id+"F17.opExtrude","SWEPT_EDGE",EDGE,{"disambiguationData":[OSD([subQ1,subQ0]),TDD([subQ4])]})]}),makeQuery(id+"F20.opExtrude","SWEPT_EDGE",EDGE,{"disambiguationData":[OSD([subQ1,subQ0]),TDD([subQ5])]})]}),makeQuery(id+"F23.opExtrude","SWEPT_EDGE",EDGE,{"disambiguationData":[OSD([subQ1,subQ0]),TDD([subQ6])]})]}),makeQuery(id+"F29.opExtrude","SWEPT_EDGE",EDGE,{"disambiguationData":[OSD([subQ1,subQ0]),TDD([makeQuery(id+"F23.opExtrude","CAP_VERTEX",VERTEX,{"disambiguationData":[OSD([subQ1,subQ0]),TDD([subQ6])],"isStart":false})])]})]})])]})]});}
            fillet(context, id + "F38", {"entities" : qUnion([Q0, Q1]), "radius" : 3 * mm, "tangentPropagation" : true, "allowEdgeOverflow" : false});
        }
    });
